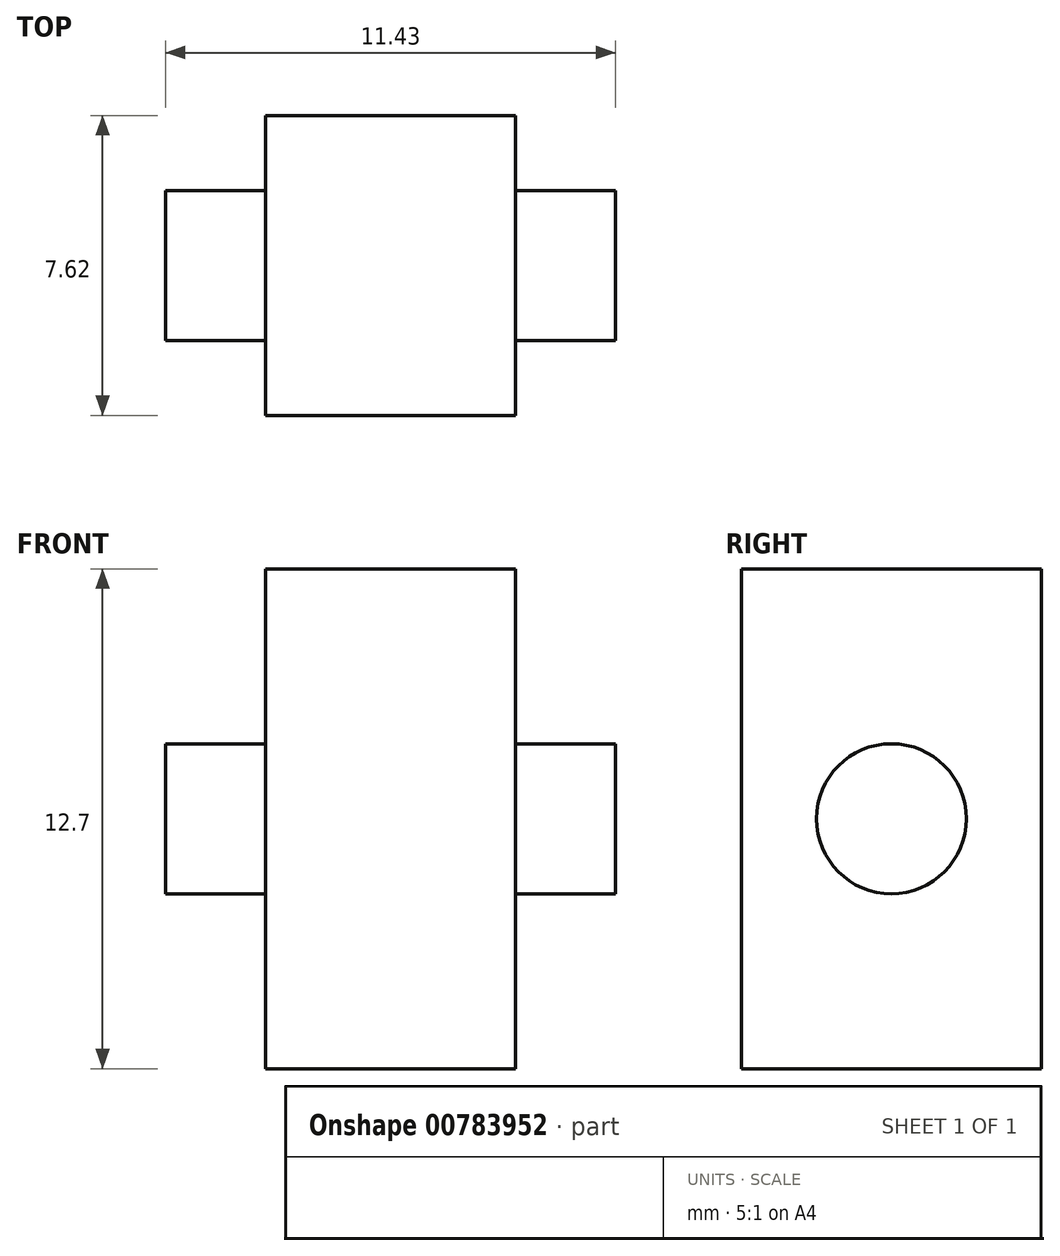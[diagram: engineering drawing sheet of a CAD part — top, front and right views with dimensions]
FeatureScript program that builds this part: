
annotation { "Feature Type Name" : "Feature", "Feature Type Description" : "" }
export const myFeature = defineFeature(function(context is Context, id is Id, definition is map)
    precondition{}
    {
        {
            var Q0;
            Q0=qCreatedBy(makeId("Top.planeOp"),FACE);
            var sketch = newSketch(context, id + "F0", { "sketchPlane" : qUnion([Q0])});
            skLineSegment(sketch, "E0", {"start": v(0, 0) * mm, "end": v(6.35, 0) * mm});
            skLineSegment(sketch, "E1", {"start": v(0, 0) * mm, "end": v(0, -7.62) * mm});
            skLineSegment(sketch, "E2", {"start": v(0, -7.62) * mm, "end": v(6.35, -7.62) * mm});
            skLineSegment(sketch, "E3", {"start": v(6.35, -7.62) * mm, "end": v(6.35, 0) * mm});
            skSolve(sketch);
        }
        {
            var Q0;
            Q0 = qSketchRegion(id + "F0", true);
            extrude(context, id + "F1", {"entities" : qUnion([Q0]), "depth" : 12.7 * mm, "offsetDistance" : 25.4 * mm});
        }
        {
            var Q0;
            Q0=makeQuery(id+"F1.opExtrude","SWEPT_FACE",FACE,{"disambiguationData":[OSD([sQuery(id+"F0.wireOp",EDGE,"E3")])]});
            var sketch = newSketch(context, id + "F2", { "sketchPlane" : qUnion([Q0])});
            skLineSegment(sketch, "E4", {"start": v(-7.62, 6.35) * mm, "end": v(0, 6.35) * mm});
            skLineSegment(sketch, "E5", {"start": v(0, 6.35) * mm, "end": v(-3.81, 6.35) * mm});
            skCircle(sketch, "E6", {"center": v(-3.81, 6.35) * mm, "radius": 1.9 * mm});
            skSolve(sketch);
        }
        {
            var Q0;
            Q0 = qSketchRegion(id + "F2", true);
            extrude(context, id + "F3", {"entities" : qUnion([Q0]), "operationType" : NewBodyOperationType.ADD, "depth" : 2.54 * mm, "offsetDistance" : 25.4 * mm});
        }
        {
            var Q0;
            Q0=makeQuery(id+"F1.opExtrude","SWEPT_FACE",FACE,{"disambiguationData":[OSD([sQuery(id+"F0.wireOp",EDGE,"E1")])]});
            var sketch = newSketch(context, id + "F4", { "sketchPlane" : qUnion([Q0])});
            skLineSegment(sketch, "E7", {"start": v(0, 6.35) * mm, "end": v(7.62, 6.35) * mm});
            skLineSegment(sketch, "E8", {"start": v(7.62, 6.35) * mm, "end": v(3.81, 6.35) * mm});
            skCircle(sketch, "E9", {"center": v(3.81, 6.35) * mm, "radius": 1.9 * mm});
            skSolve(sketch);
        }
        {
            var Q0;
            Q0 = qSketchRegion(id + "F4", true);
            extrude(context, id + "F5", {"entities" : qUnion([Q0]), "operationType" : NewBodyOperationType.ADD, "depth" : 2.54 * mm, "offsetDistance" : 25.4 * mm});
        }
    });
